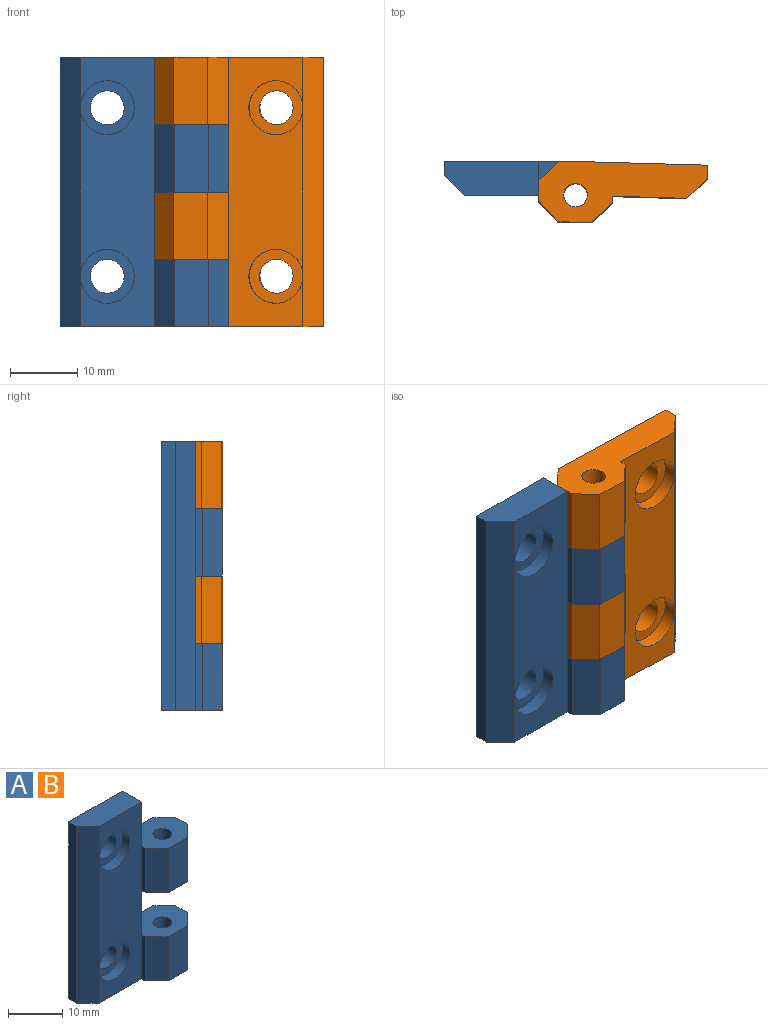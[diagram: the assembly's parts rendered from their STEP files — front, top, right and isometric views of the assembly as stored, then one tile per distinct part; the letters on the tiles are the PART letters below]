
ASSEMBLY  parts=2 mates=1
PART A: 31 faces, bbox 25x9x40 mm
  f0: cylinder r=2.5mm len=5mm, axis (0,-1,0), area 47.1mm2, adj f3,f30
  f1: cylinder r=2.5mm len=5mm, axis (0,-1,0), area 47.1mm2, adj f3,f27
  f2: plane 40x11mm, normal (0,-1,0), area 339.5mm2, adj f6,f8,f10,f13,f14,f16,f24,f28
  f3: plane 40x22mm, normal (0,1,0), area 680.7mm2, adj f0,f1,f6,f7,f8,f9,f10,f11
  f4: plane 10x3mm, normal (1,0,0), area 30mm2, adj f9,f12,f19,f21
  f5: plane 10x3mm, normal (1,0,0), area 30mm2, adj f8,f11,f18,f23
  f6: plane 14x5mm, normal (0,0,1), area 65.5mm2, adj f2,f3,f7,f13,f24
  f7: plane 40x2mm, normal (-1,0,0), area 80mm2, adj f3,f6,f8,f24
  f8: plane 25x9mm, normal (0,0,-1), area 141.4mm2, adj f2,f3,f5,f7,f16,f17,f18,f22
  f9: plane 11x9mm, normal (0,0,-1), area 75.9mm2, adj f3,f4,f10,f14,f15,f19,f20,f21
  f10: plane 10x5mm, normal (1,0,0), area 50mm2, adj f2,f3,f9,f11
  f11: plane 11x9mm, normal (0,0,1), area 75.9mm2, adj f3,f5,f10,f16,f17,f18,f22,f23
  f12: plane 11x9mm, normal (0,0,1), area 75.9mm2, adj f3,f4,f13,f14,f15,f19,f20,f21
  f13: plane 10x5mm, normal (1,0,0), area 50mm2, adj f2,f3,f6,f12
  f14: plane 10x1mm, normal (-1,0,0), area 10mm2, adj f2,f9,f12,f20
  f15: plane 10x5mm, normal (0,-1,0), area 50mm2, adj f9,f12,f20,f21
  f16: plane 10x1mm, normal (-1,0,0), area 10mm2, adj f2,f8,f11,f22
  f17: plane 10x5mm, normal (0,-1,0), area 50mm2, adj f8,f11,f22,f23
  f18: plane 10x3mm, normal (0.71,0.71,0), area 42.4mm2, adj f3,f5,f8,f11
  f19: plane 10x3mm, normal (0.71,0.71,0), area 42.4mm2, adj f3,f4,f9,f12
  f20: plane 10x3mm, normal (-0.71,-0.71,0), area 42.4mm2, adj f9,f12,f14,f15
  f21: plane 10x3mm, normal (0.71,-0.71,0), area 42.4mm2, adj f4,f9,f12,f15
  f22: plane 10x3mm, normal (-0.71,-0.71,0), area 42.4mm2, adj f8,f11,f16,f17
  f23: plane 10x3mm, normal (0.71,-0.71,0), area 42.4mm2, adj f5,f8,f11,f17
  f24: plane 40x3mm, normal (-0.71,-0.71,0), area 169.7mm2, adj f2,f6,f7,f8
  f25: cylinder r=1.75mm len=10mm, axis (0,0,-1), area 110mm2, adj f9,f12
  f26: cylinder r=1.75mm len=10mm, axis (0,0,-1), area 110mm2, adj f8,f11
  f27: plane 8x8mm, normal (0,-1,0), area 30.6mm2, adj f1,f28
  f28: cylinder r=4mm len=8mm, axis (0,-1,0), area 50.3mm2, adj f2,f27
  f29: cylinder r=4mm len=8mm, axis (0,-1,0), area 50.3mm2, adj f2,f30
  f30: plane 8x8mm, normal (0,-1,0), area 30.6mm2, adj f0,f29
PART B: same geometry as A
PLACE A t=(-41.02,-6.43,0.51)mm fixed
PLACE B rot(axis=(-0.01,-1,0),180deg) t=(-26.88,-6.63,0.51)mm
MATE revolute A.f25 <-> B.f25  axis (0,0,1) through (-34.02,-11.43,-9.49)mm
